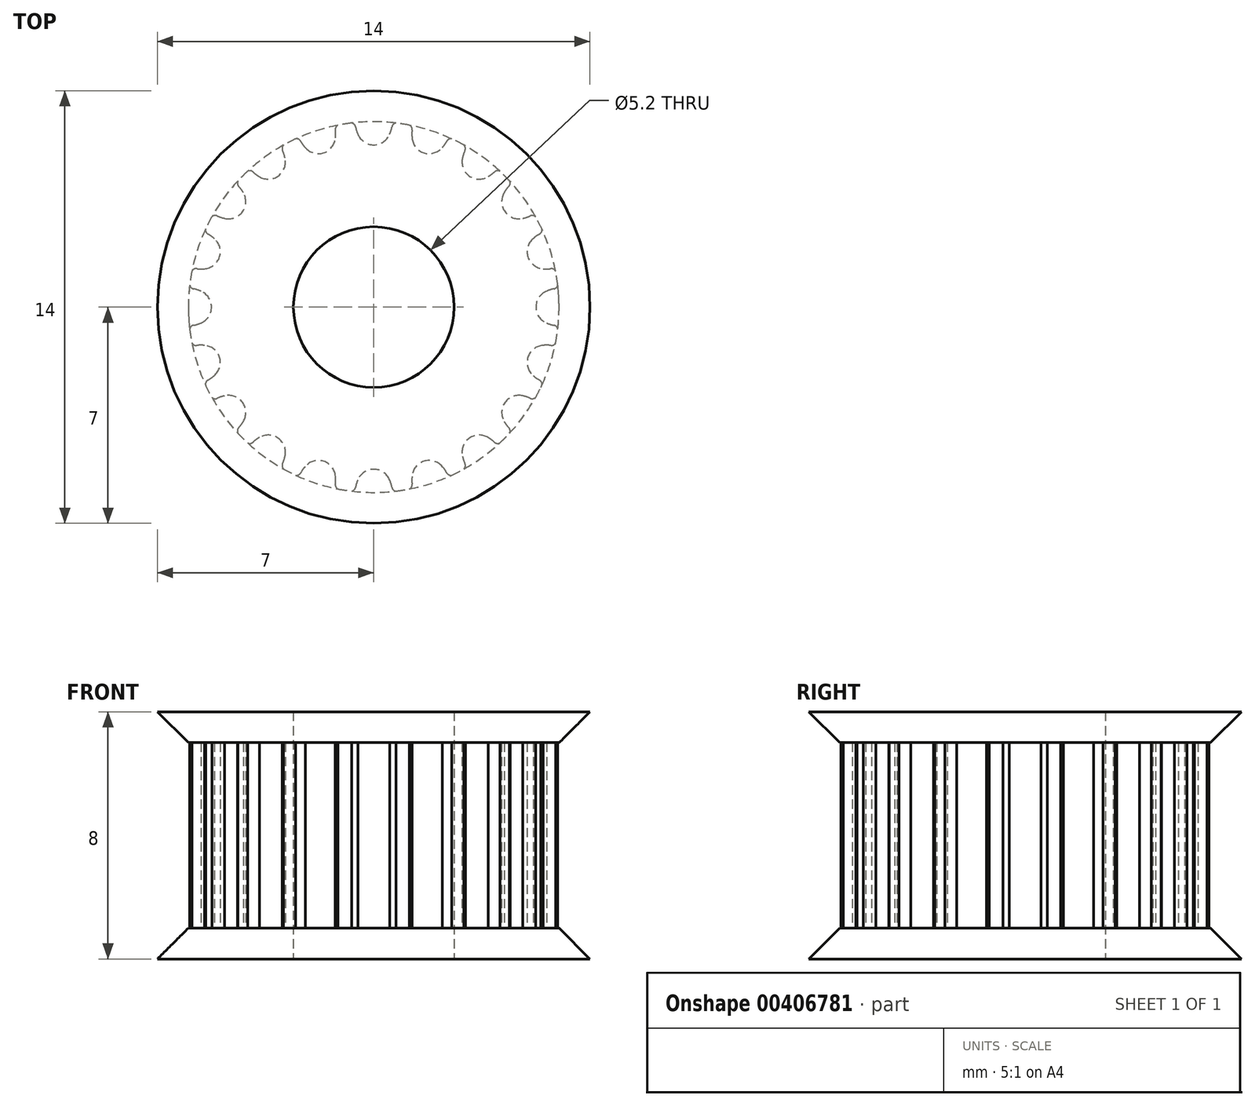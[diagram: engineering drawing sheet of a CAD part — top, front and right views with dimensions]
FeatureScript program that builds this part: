
annotation { "Feature Type Name" : "Feature", "Feature Type Description" : "" }
export const myFeature = defineFeature(function(context is Context, id is Id, definition is map)
    precondition{}
    {
        {
            var Q0;
            Q0=qCreatedBy(makeId("Top.planeOp"),FACE);
            var sketch = newSketch(context, id + "F0", { "sketchPlane" : qUnion([Q0])});
            skLineSegment(sketch, "E0", {"start": v(-19.17, 17.78) * mm, "end": v(-18.17, 17.78) * mm});
            skLineSegment(sketch, "E1", {"start": v(-18.17, 17.78) * mm, "end": v(-18.17, 18.4) * mm});
            skArc(sketch, "E2", {"start": v(-18.67, 18.85) * mm, "mid": v(-18.88, 19.07) * mm, "end": v(-19.17, 19.16) * mm});
            skArc(sketch, "E3", {"start": v(-18.58, 18.54) * mm, "mid": v(-18.61, 18.7) * mm, "end": v(-18.67, 18.85) * mm});
            skArc(sketch, "E4", {"start": v(-18.58, 18.54) * mm, "mid": v(-18.53, 18.44) * mm, "end": v(-18.43, 18.4) * mm});
            skLineSegment(sketch, "E5", {"start": v(-18.43, 18.4) * mm, "end": v(-18.17, 18.4) * mm});
            skArc(sketch, "E6.0.MirrorCS", {"start": v(-19.67, 18.85) * mm, "mid": v(-19.47, 19.07) * mm, "end": v(-19.17, 19.16) * mm});
            skArc(sketch, "E7.0.MirrorCS", {"start": v(-19.76, 18.54) * mm, "mid": v(-19.73, 18.7) * mm, "end": v(-19.67, 18.85) * mm});
            skArc(sketch, "E8.0.MirrorCS", {"start": v(-19.76, 18.54) * mm, "mid": v(-19.81, 18.44) * mm, "end": v(-19.91, 18.4) * mm});
            skLineSegment(sketch, "E9.0.MirrorCS", {"start": v(-19.91, 18.4) * mm, "end": v(-20.17, 18.4) * mm});
            skLineSegment(sketch, "E10.0.MirrorCS", {"start": v(-20.17, 17.78) * mm, "end": v(-20.17, 18.4) * mm});
            skLineSegment(sketch, "E11.0.MirrorCS", {"start": v(-19.17, 17.78) * mm, "end": v(-20.17, 17.78) * mm});
            skLineSegment(sketch, "E12.direction1", {"start": v(-20.17, 17.78) * mm, "end": v(-18.17, 17.78) * mm, "construction": true});
            skLineSegment(sketch, "E13", {"start": v(-20.17, 18.15) * mm, "end": v(-18.17, 18.15) * mm, "construction": true});
            skPoint(sketch, "E14", {"position": v(0, -5.25) * mm});
            skArc(sketch, "E15", {"start": v(0.51, -5.6) * mm, "mid": v(0, -5.25) * mm, "end": v(-0.51, -5.6) * mm});
            skArc(sketch, "E16", {"start": v(-0.51, -5.6) * mm, "mid": v(-0.56, -5.71) * mm, "end": v(-0.59, -5.83) * mm});
            skArc(sketch, "E17", {"start": v(0.59, -5.83) * mm, "mid": v(0.56, -5.71) * mm, "end": v(0.51, -5.6) * mm});
            skArc(sketch, "E18", {"start": v(0.72, -5.96) * mm, "mid": v(0.94, -5.93) * mm, "end": v(1.16, -5.89) * mm});
            skArc(sketch, "E19", {"start": v(0.59, -5.83) * mm, "mid": v(0.66, -5.94) * mm, "end": v(0.8, -5.95) * mm});
            skArc(sketch, "E20", {"start": v(-0.59, -5.83) * mm, "mid": v(-0.66, -5.94) * mm, "end": v(-0.8, -5.95) * mm});
            skArc(sketch, "E21.1.0", {"start": v(2.22, -5.16) * mm, "mid": v(1.62, -5) * mm, "end": v(1.24, -5.48) * mm});
            skPoint(sketch, "E21.1.1", {"position": v(1.62, -5) * mm});
            skArc(sketch, "E21.1.2", {"start": v(1.24, -5.48) * mm, "mid": v(1.23, -5.6) * mm, "end": v(1.24, -5.73) * mm});
            skArc(sketch, "E21.1.3", {"start": v(2.36, -5.37) * mm, "mid": v(2.47, -5.44) * mm, "end": v(2.6, -5.41) * mm});
            skArc(sketch, "E21.1.4", {"start": v(1.24, -5.73) * mm, "mid": v(1.2, -5.85) * mm, "end": v(1.08, -5.9) * mm});
            skArc(sketch, "E21.1.5", {"start": v(2.36, -5.37) * mm, "mid": v(2.3, -5.26) * mm, "end": v(2.22, -5.16) * mm});
            skArc(sketch, "E22.3.2.0", {"start": v(3.7, -4.22) * mm, "mid": v(3.09, -4.25) * mm, "end": v(2.87, -4.83) * mm});
            skPoint(sketch, "E22.4.2.0", {"position": v(3.09, -4.25) * mm});
            skArc(sketch, "E22.5.2.0", {"start": v(2.87, -4.83) * mm, "mid": v(2.9, -4.95) * mm, "end": v(2.95, -5.07) * mm});
            skArc(sketch, "E22.9.2.0", {"start": v(3.9, -4.37) * mm, "mid": v(4.03, -4.41) * mm, "end": v(4.14, -4.35) * mm});
            skArc(sketch, "E22.13.2.0", {"start": v(2.95, -5.07) * mm, "mid": v(2.95, -5.2) * mm, "end": v(2.85, -5.28) * mm});
            skArc(sketch, "E22.17.2.0", {"start": v(3.9, -4.37) * mm, "mid": v(3.81, -4.3) * mm, "end": v(3.7, -4.22) * mm});
            skArc(sketch, "E22.3.3.0", {"start": v(4.83, -2.87) * mm, "mid": v(4.25, -3.09) * mm, "end": v(4.22, -3.7) * mm});
            skPoint(sketch, "E22.4.3.0", {"position": v(4.25, -3.09) * mm});
            skArc(sketch, "E22.5.3.0", {"start": v(4.22, -3.7) * mm, "mid": v(4.3, -3.81) * mm, "end": v(4.37, -3.9) * mm});
            skArc(sketch, "E22.9.3.0", {"start": v(5.07, -2.95) * mm, "mid": v(5.2, -2.95) * mm, "end": v(5.28, -2.85) * mm});
            skArc(sketch, "E22.13.3.0", {"start": v(4.37, -3.9) * mm, "mid": v(4.41, -4.03) * mm, "end": v(4.35, -4.14) * mm});
            skArc(sketch, "E22.17.3.0", {"start": v(5.07, -2.95) * mm, "mid": v(4.95, -2.9) * mm, "end": v(4.83, -2.87) * mm});
            skArc(sketch, "E22.3.4.0", {"start": v(5.48, -1.24) * mm, "mid": v(5, -1.62) * mm, "end": v(5.16, -2.22) * mm});
            skPoint(sketch, "E22.4.4.0", {"position": v(5, -1.62) * mm});
            skArc(sketch, "E22.5.4.0", {"start": v(5.16, -2.22) * mm, "mid": v(5.26, -2.3) * mm, "end": v(5.37, -2.36) * mm});
            skArc(sketch, "E22.9.4.0", {"start": v(5.73, -1.24) * mm, "mid": v(5.85, -1.2) * mm, "end": v(5.9, -1.08) * mm});
            skArc(sketch, "E22.13.4.0", {"start": v(5.37, -2.36) * mm, "mid": v(5.44, -2.47) * mm, "end": v(5.41, -2.6) * mm});
            skArc(sketch, "E22.17.4.0", {"start": v(5.73, -1.24) * mm, "mid": v(5.6, -1.23) * mm, "end": v(5.48, -1.24) * mm});
            skArc(sketch, "E22.3.5.0", {"start": v(5.6, 0.51) * mm, "mid": v(5.25, 0) * mm, "end": v(5.6, -0.51) * mm});
            skPoint(sketch, "E22.4.5.0", {"position": v(5.25, 0) * mm});
            skArc(sketch, "E22.5.5.0", {"start": v(5.6, -0.51) * mm, "mid": v(5.71, -0.56) * mm, "end": v(5.83, -0.59) * mm});
            skArc(sketch, "E22.9.5.0", {"start": v(5.83, 0.59) * mm, "mid": v(5.94, 0.66) * mm, "end": v(5.95, 0.8) * mm});
            skArc(sketch, "E22.13.5.0", {"start": v(5.83, -0.59) * mm, "mid": v(5.94, -0.66) * mm, "end": v(5.95, -0.8) * mm});
            skArc(sketch, "E22.17.5.0", {"start": v(5.83, 0.59) * mm, "mid": v(5.71, 0.56) * mm, "end": v(5.6, 0.51) * mm});
            skArc(sketch, "E22.3.6.0", {"start": v(5.16, 2.22) * mm, "mid": v(5, 1.62) * mm, "end": v(5.48, 1.24) * mm});
            skPoint(sketch, "E22.4.6.0", {"position": v(5, 1.62) * mm});
            skArc(sketch, "E22.5.6.0", {"start": v(5.48, 1.24) * mm, "mid": v(5.6, 1.23) * mm, "end": v(5.73, 1.24) * mm});
            skArc(sketch, "E22.9.6.0", {"start": v(5.37, 2.36) * mm, "mid": v(5.44, 2.47) * mm, "end": v(5.41, 2.6) * mm});
            skArc(sketch, "E22.13.6.0", {"start": v(5.73, 1.24) * mm, "mid": v(5.85, 1.2) * mm, "end": v(5.9, 1.08) * mm});
            skArc(sketch, "E22.17.6.0", {"start": v(5.37, 2.36) * mm, "mid": v(5.26, 2.3) * mm, "end": v(5.16, 2.22) * mm});
            skArc(sketch, "E22.3.7.0", {"start": v(4.22, 3.7) * mm, "mid": v(4.25, 3.09) * mm, "end": v(4.83, 2.87) * mm});
            skPoint(sketch, "E22.4.7.0", {"position": v(4.25, 3.09) * mm});
            skArc(sketch, "E22.5.7.0", {"start": v(4.83, 2.87) * mm, "mid": v(4.95, 2.9) * mm, "end": v(5.07, 2.95) * mm});
            skArc(sketch, "E22.9.7.0", {"start": v(4.37, 3.9) * mm, "mid": v(4.41, 4.03) * mm, "end": v(4.35, 4.14) * mm});
            skArc(sketch, "E22.13.7.0", {"start": v(5.07, 2.95) * mm, "mid": v(5.2, 2.95) * mm, "end": v(5.28, 2.85) * mm});
            skArc(sketch, "E22.17.7.0", {"start": v(4.37, 3.9) * mm, "mid": v(4.3, 3.81) * mm, "end": v(4.22, 3.7) * mm});
            skArc(sketch, "E22.3.8.0", {"start": v(2.87, 4.83) * mm, "mid": v(3.09, 4.25) * mm, "end": v(3.7, 4.22) * mm});
            skPoint(sketch, "E22.4.8.0", {"position": v(3.09, 4.25) * mm});
            skArc(sketch, "E22.5.8.0", {"start": v(3.7, 4.22) * mm, "mid": v(3.81, 4.3) * mm, "end": v(3.9, 4.37) * mm});
            skArc(sketch, "E22.9.8.0", {"start": v(2.95, 5.07) * mm, "mid": v(2.95, 5.2) * mm, "end": v(2.85, 5.28) * mm});
            skArc(sketch, "E22.13.8.0", {"start": v(3.9, 4.37) * mm, "mid": v(4.03, 4.41) * mm, "end": v(4.14, 4.35) * mm});
            skArc(sketch, "E22.17.8.0", {"start": v(2.95, 5.07) * mm, "mid": v(2.9, 4.95) * mm, "end": v(2.87, 4.83) * mm});
            skArc(sketch, "E22.3.9.0", {"start": v(1.24, 5.48) * mm, "mid": v(1.62, 5) * mm, "end": v(2.22, 5.16) * mm});
            skPoint(sketch, "E22.4.9.0", {"position": v(1.62, 5) * mm});
            skArc(sketch, "E22.5.9.0", {"start": v(2.22, 5.16) * mm, "mid": v(2.3, 5.26) * mm, "end": v(2.36, 5.37) * mm});
            skArc(sketch, "E22.9.9.0", {"start": v(1.24, 5.73) * mm, "mid": v(1.2, 5.85) * mm, "end": v(1.08, 5.9) * mm});
            skArc(sketch, "E22.13.9.0", {"start": v(2.36, 5.37) * mm, "mid": v(2.47, 5.44) * mm, "end": v(2.6, 5.41) * mm});
            skArc(sketch, "E22.17.9.0", {"start": v(1.24, 5.73) * mm, "mid": v(1.23, 5.6) * mm, "end": v(1.24, 5.48) * mm});
            skArc(sketch, "E22.3.10.0", {"start": v(-0.51, 5.6) * mm, "mid": v(0, 5.25) * mm, "end": v(0.51, 5.6) * mm});
            skPoint(sketch, "E22.4.10.0", {"position": v(0, 5.25) * mm});
            skArc(sketch, "E22.5.10.0", {"start": v(0.51, 5.6) * mm, "mid": v(0.56, 5.71) * mm, "end": v(0.59, 5.83) * mm});
            skArc(sketch, "E22.9.10.0", {"start": v(-0.59, 5.83) * mm, "mid": v(-0.66, 5.94) * mm, "end": v(-0.8, 5.95) * mm});
            skArc(sketch, "E22.13.10.0", {"start": v(0.59, 5.83) * mm, "mid": v(0.66, 5.94) * mm, "end": v(0.8, 5.95) * mm});
            skArc(sketch, "E22.17.10.0", {"start": v(-0.59, 5.83) * mm, "mid": v(-0.56, 5.71) * mm, "end": v(-0.51, 5.6) * mm});
            skArc(sketch, "E22.3.11.0", {"start": v(-2.22, 5.16) * mm, "mid": v(-1.62, 5) * mm, "end": v(-1.24, 5.48) * mm});
            skPoint(sketch, "E22.4.11.0", {"position": v(-1.62, 5) * mm});
            skArc(sketch, "E22.5.11.0", {"start": v(-1.24, 5.48) * mm, "mid": v(-1.23, 5.6) * mm, "end": v(-1.24, 5.73) * mm});
            skArc(sketch, "E22.9.11.0", {"start": v(-2.36, 5.37) * mm, "mid": v(-2.47, 5.44) * mm, "end": v(-2.6, 5.41) * mm});
            skArc(sketch, "E22.13.11.0", {"start": v(-1.24, 5.73) * mm, "mid": v(-1.2, 5.85) * mm, "end": v(-1.08, 5.9) * mm});
            skArc(sketch, "E22.17.11.0", {"start": v(-2.36, 5.37) * mm, "mid": v(-2.3, 5.26) * mm, "end": v(-2.22, 5.16) * mm});
            skArc(sketch, "E22.3.12.0", {"start": v(-3.7, 4.22) * mm, "mid": v(-3.09, 4.25) * mm, "end": v(-2.87, 4.83) * mm});
            skPoint(sketch, "E22.4.12.0", {"position": v(-3.09, 4.25) * mm});
            skArc(sketch, "E22.5.12.0", {"start": v(-2.87, 4.83) * mm, "mid": v(-2.9, 4.95) * mm, "end": v(-2.95, 5.07) * mm});
            skArc(sketch, "E22.9.12.0", {"start": v(-3.9, 4.37) * mm, "mid": v(-4.03, 4.41) * mm, "end": v(-4.14, 4.35) * mm});
            skArc(sketch, "E22.13.12.0", {"start": v(-2.95, 5.07) * mm, "mid": v(-2.95, 5.2) * mm, "end": v(-2.85, 5.28) * mm});
            skArc(sketch, "E22.17.12.0", {"start": v(-3.9, 4.37) * mm, "mid": v(-3.81, 4.3) * mm, "end": v(-3.7, 4.22) * mm});
            skArc(sketch, "E22.3.13.0", {"start": v(-4.83, 2.87) * mm, "mid": v(-4.25, 3.09) * mm, "end": v(-4.22, 3.7) * mm});
            skPoint(sketch, "E22.4.13.0", {"position": v(-4.25, 3.09) * mm});
            skArc(sketch, "E22.5.13.0", {"start": v(-4.22, 3.7) * mm, "mid": v(-4.3, 3.81) * mm, "end": v(-4.37, 3.9) * mm});
            skArc(sketch, "E22.9.13.0", {"start": v(-5.07, 2.95) * mm, "mid": v(-5.2, 2.95) * mm, "end": v(-5.28, 2.85) * mm});
            skArc(sketch, "E22.13.13.0", {"start": v(-4.37, 3.9) * mm, "mid": v(-4.41, 4.03) * mm, "end": v(-4.35, 4.14) * mm});
            skArc(sketch, "E22.17.13.0", {"start": v(-5.07, 2.95) * mm, "mid": v(-4.95, 2.9) * mm, "end": v(-4.83, 2.87) * mm});
            skArc(sketch, "E22.3.14.0", {"start": v(-5.48, 1.24) * mm, "mid": v(-5, 1.62) * mm, "end": v(-5.16, 2.22) * mm});
            skPoint(sketch, "E22.4.14.0", {"position": v(-5, 1.62) * mm});
            skArc(sketch, "E22.5.14.0", {"start": v(-5.16, 2.22) * mm, "mid": v(-5.26, 2.3) * mm, "end": v(-5.37, 2.36) * mm});
            skArc(sketch, "E22.9.14.0", {"start": v(-5.73, 1.24) * mm, "mid": v(-5.85, 1.2) * mm, "end": v(-5.9, 1.08) * mm});
            skArc(sketch, "E22.13.14.0", {"start": v(-5.37, 2.36) * mm, "mid": v(-5.44, 2.47) * mm, "end": v(-5.41, 2.6) * mm});
            skArc(sketch, "E22.17.14.0", {"start": v(-5.73, 1.24) * mm, "mid": v(-5.6, 1.23) * mm, "end": v(-5.48, 1.24) * mm});
            skArc(sketch, "E22.3.15.0", {"start": v(-5.6, -0.51) * mm, "mid": v(-5.25, 0) * mm, "end": v(-5.6, 0.51) * mm});
            skPoint(sketch, "E22.4.15.0", {"position": v(-5.25, 0) * mm});
            skArc(sketch, "E22.5.15.0", {"start": v(-5.6, 0.51) * mm, "mid": v(-5.71, 0.56) * mm, "end": v(-5.83, 0.59) * mm});
            skArc(sketch, "E22.9.15.0", {"start": v(-5.83, -0.59) * mm, "mid": v(-5.94, -0.66) * mm, "end": v(-5.95, -0.8) * mm});
            skArc(sketch, "E22.13.15.0", {"start": v(-5.83, 0.59) * mm, "mid": v(-5.94, 0.66) * mm, "end": v(-5.95, 0.8) * mm});
            skArc(sketch, "E22.17.15.0", {"start": v(-5.83, -0.59) * mm, "mid": v(-5.71, -0.56) * mm, "end": v(-5.6, -0.51) * mm});
            skArc(sketch, "E22.3.16.0", {"start": v(-5.16, -2.22) * mm, "mid": v(-5, -1.62) * mm, "end": v(-5.48, -1.24) * mm});
            skPoint(sketch, "E22.4.16.0", {"position": v(-5, -1.62) * mm});
            skArc(sketch, "E22.5.16.0", {"start": v(-5.48, -1.24) * mm, "mid": v(-5.6, -1.23) * mm, "end": v(-5.73, -1.24) * mm});
            skArc(sketch, "E22.9.16.0", {"start": v(-5.37, -2.36) * mm, "mid": v(-5.44, -2.47) * mm, "end": v(-5.41, -2.6) * mm});
            skArc(sketch, "E22.13.16.0", {"start": v(-5.73, -1.24) * mm, "mid": v(-5.85, -1.2) * mm, "end": v(-5.9, -1.08) * mm});
            skArc(sketch, "E22.17.16.0", {"start": v(-5.37, -2.36) * mm, "mid": v(-5.26, -2.3) * mm, "end": v(-5.16, -2.22) * mm});
            skArc(sketch, "E22.3.17.0", {"start": v(-4.22, -3.7) * mm, "mid": v(-4.25, -3.09) * mm, "end": v(-4.83, -2.87) * mm});
            skPoint(sketch, "E22.4.17.0", {"position": v(-4.25, -3.09) * mm});
            skArc(sketch, "E22.5.17.0", {"start": v(-4.83, -2.87) * mm, "mid": v(-4.95, -2.9) * mm, "end": v(-5.07, -2.95) * mm});
            skArc(sketch, "E22.9.17.0", {"start": v(-4.37, -3.9) * mm, "mid": v(-4.41, -4.03) * mm, "end": v(-4.35, -4.14) * mm});
            skArc(sketch, "E22.13.17.0", {"start": v(-5.07, -2.95) * mm, "mid": v(-5.2, -2.95) * mm, "end": v(-5.28, -2.85) * mm});
            skArc(sketch, "E22.17.17.0", {"start": v(-4.37, -3.9) * mm, "mid": v(-4.3, -3.81) * mm, "end": v(-4.22, -3.7) * mm});
            skArc(sketch, "E22.3.18.0", {"start": v(-2.87, -4.83) * mm, "mid": v(-3.09, -4.25) * mm, "end": v(-3.7, -4.22) * mm});
            skPoint(sketch, "E22.4.18.0", {"position": v(-3.09, -4.25) * mm});
            skArc(sketch, "E22.5.18.0", {"start": v(-3.7, -4.22) * mm, "mid": v(-3.81, -4.3) * mm, "end": v(-3.9, -4.37) * mm});
            skArc(sketch, "E22.9.18.0", {"start": v(-2.95, -5.07) * mm, "mid": v(-2.95, -5.2) * mm, "end": v(-2.85, -5.28) * mm});
            skArc(sketch, "E22.13.18.0", {"start": v(-3.9, -4.37) * mm, "mid": v(-4.03, -4.41) * mm, "end": v(-4.14, -4.35) * mm});
            skArc(sketch, "E22.17.18.0", {"start": v(-2.95, -5.07) * mm, "mid": v(-2.9, -4.95) * mm, "end": v(-2.87, -4.83) * mm});
            skArc(sketch, "E22.3.19.0", {"start": v(-1.24, -5.48) * mm, "mid": v(-1.62, -5) * mm, "end": v(-2.22, -5.16) * mm});
            skPoint(sketch, "E22.4.19.0", {"position": v(-1.62, -5) * mm});
            skArc(sketch, "E22.5.19.0", {"start": v(-2.22, -5.16) * mm, "mid": v(-2.3, -5.26) * mm, "end": v(-2.36, -5.37) * mm});
            skArc(sketch, "E22.9.19.0", {"start": v(-1.24, -5.73) * mm, "mid": v(-1.2, -5.85) * mm, "end": v(-1.08, -5.9) * mm});
            skArc(sketch, "E22.13.19.0", {"start": v(-2.36, -5.37) * mm, "mid": v(-2.47, -5.44) * mm, "end": v(-2.6, -5.41) * mm});
            skArc(sketch, "E22.17.19.0", {"start": v(-1.24, -5.73) * mm, "mid": v(-1.23, -5.6) * mm, "end": v(-1.24, -5.48) * mm});
            skArc(sketch, "E23.trimOffspring", {"start": v(2.52, -5.44) * mm, "mid": v(2.72, -5.35) * mm, "end": v(2.92, -5.24) * mm});
            skArc(sketch, "E24.trimOffspring", {"start": v(4.08, -4.4) * mm, "mid": v(4.24, -4.24) * mm, "end": v(4.4, -4.08) * mm});
            skArc(sketch, "E25.trimOffspring", {"start": v(5.24, -2.92) * mm, "mid": v(5.33, -2.76) * mm, "end": v(5.41, -2.6) * mm});
            skArc(sketch, "E26.trimOffspring", {"start": v(5.89, -1.16) * mm, "mid": v(5.93, -0.94) * mm, "end": v(5.96, -0.72) * mm});
            skArc(sketch, "E27.trimOffspring", {"start": v(5.44, 2.52) * mm, "mid": v(5.35, 2.72) * mm, "end": v(5.24, 2.92) * mm});
            skArc(sketch, "E28.trimOffspring", {"start": v(4.4, 4.08) * mm, "mid": v(4.24, 4.24) * mm, "end": v(4.08, 4.4) * mm});
            skArc(sketch, "E29.trimOffspring", {"start": v(5.96, 0.72) * mm, "mid": v(5.93, 0.94) * mm, "end": v(5.89, 1.16) * mm});
            skArc(sketch, "E30.trimOffspring", {"start": v(2.92, 5.24) * mm, "mid": v(2.72, 5.35) * mm, "end": v(2.52, 5.44) * mm});
            skArc(sketch, "E31.trimOffspring", {"start": v(1.16, 5.89) * mm, "mid": v(0.94, 5.93) * mm, "end": v(0.72, 5.96) * mm});
            skArc(sketch, "E32.trimOffspring", {"start": v(-0.72, 5.96) * mm, "mid": v(-0.94, 5.93) * mm, "end": v(-1.16, 5.89) * mm});
            skArc(sketch, "E33.trimOffspring", {"start": v(-2.52, 5.44) * mm, "mid": v(-2.72, 5.35) * mm, "end": v(-2.92, 5.24) * mm});
            skArc(sketch, "E34.trimOffspring", {"start": v(-4.08, 4.4) * mm, "mid": v(-4.24, 4.24) * mm, "end": v(-4.4, 4.08) * mm});
            skArc(sketch, "E35.trimOffspring", {"start": v(-5.24, 2.92) * mm, "mid": v(-5.35, 2.72) * mm, "end": v(-5.44, 2.52) * mm});
            skArc(sketch, "E36.trimOffspring", {"start": v(-5.89, 1.16) * mm, "mid": v(-5.93, 0.94) * mm, "end": v(-5.96, 0.72) * mm});
            skArc(sketch, "E37.trimOffspring", {"start": v(-5.96, -0.72) * mm, "mid": v(-5.93, -0.94) * mm, "end": v(-5.89, -1.16) * mm});
            skArc(sketch, "E38.trimOffspring", {"start": v(-5.44, -2.52) * mm, "mid": v(-5.35, -2.72) * mm, "end": v(-5.24, -2.92) * mm});
            skArc(sketch, "E39.trimOffspring", {"start": v(-4.4, -4.08) * mm, "mid": v(-4.24, -4.24) * mm, "end": v(-4.08, -4.4) * mm});
            skArc(sketch, "E40.trimOffspring", {"start": v(-2.92, -5.24) * mm, "mid": v(-2.72, -5.35) * mm, "end": v(-2.52, -5.44) * mm});
            skArc(sketch, "E41.trimOffspring", {"start": v(-1.16, -5.89) * mm, "mid": v(-0.94, -5.93) * mm, "end": v(-0.72, -5.96) * mm});
            skSolve(sketch);
        }
        {
            var Q0;
            Q0=makeQuery(id+"F0.imprint","IMPRINT",FACE,{"disambiguationData":[TD([[makeQuery(id+"F0.imprint","IMPRINT",EDGE,{"derivedFrom":sQuery(id+"F0.wireOp",EDGE,"E15")}),-1.0]])]});
            extrude(context, id + "F1", {"entities" : qUnion([Q0]), "depth" : 6 * mm});
        }
        {
            var Q0;
            Q0=makeQuery(id+"F1.opExtrude","CAP_FACE",FACE,{"disambiguationData":[OSD([sQuery(id+"F0.wireOp",EDGE,"E15"),sQuery(id+"F0.wireOp",EDGE,"E16"),sQuery(id+"F0.wireOp",EDGE,"E17"),sQuery(id+"F0.wireOp",EDGE,"E18"),sQuery(id+"F0.wireOp",EDGE,"E19"),sQuery(id+"F0.wireOp",EDGE,"E20"),sQuery(id+"F0.wireOp",EDGE,"E21.1.0"),sQuery(id+"F0.wireOp",EDGE,"E21.1.2"),sQuery(id+"F0.wireOp",EDGE,"E21.1.3"),sQuery(id+"F0.wireOp",EDGE,"E21.1.4"),sQuery(id+"F0.wireOp",EDGE,"E21.1.5"),sQuery(id+"F0.wireOp",EDGE,"E22.3.2.0"),sQuery(id+"F0.wireOp",EDGE,"E22.5.2.0"),sQuery(id+"F0.wireOp",EDGE,"E22.9.2.0"),sQuery(id+"F0.wireOp",EDGE,"E22.13.2.0"),sQuery(id+"F0.wireOp",EDGE,"E22.17.2.0"),sQuery(id+"F0.wireOp",EDGE,"E22.3.3.0"),sQuery(id+"F0.wireOp",EDGE,"E22.5.3.0"),sQuery(id+"F0.wireOp",EDGE,"E22.9.3.0"),sQuery(id+"F0.wireOp",EDGE,"E22.13.3.0"),sQuery(id+"F0.wireOp",EDGE,"E22.17.3.0"),sQuery(id+"F0.wireOp",EDGE,"E22.3.4.0"),sQuery(id+"F0.wireOp",EDGE,"E22.5.4.0"),sQuery(id+"F0.wireOp",EDGE,"E22.9.4.0"),sQuery(id+"F0.wireOp",EDGE,"E22.13.4.0"),sQuery(id+"F0.wireOp",EDGE,"E22.17.4.0"),sQuery(id+"F0.wireOp",EDGE,"E22.3.5.0"),sQuery(id+"F0.wireOp",EDGE,"E22.5.5.0"),sQuery(id+"F0.wireOp",EDGE,"E22.9.5.0"),sQuery(id+"F0.wireOp",EDGE,"E22.13.5.0"),sQuery(id+"F0.wireOp",EDGE,"E22.17.5.0"),sQuery(id+"F0.wireOp",EDGE,"E22.3.6.0"),sQuery(id+"F0.wireOp",EDGE,"E22.5.6.0"),sQuery(id+"F0.wireOp",EDGE,"E22.9.6.0"),sQuery(id+"F0.wireOp",EDGE,"E22.13.6.0"),sQuery(id+"F0.wireOp",EDGE,"E22.17.6.0"),sQuery(id+"F0.wireOp",EDGE,"E22.3.7.0"),sQuery(id+"F0.wireOp",EDGE,"E22.5.7.0"),sQuery(id+"F0.wireOp",EDGE,"E22.9.7.0"),sQuery(id+"F0.wireOp",EDGE,"E22.13.7.0"),sQuery(id+"F0.wireOp",EDGE,"E22.17.7.0"),sQuery(id+"F0.wireOp",EDGE,"E22.3.8.0"),sQuery(id+"F0.wireOp",EDGE,"E22.5.8.0"),sQuery(id+"F0.wireOp",EDGE,"E22.9.8.0"),sQuery(id+"F0.wireOp",EDGE,"E22.13.8.0"),sQuery(id+"F0.wireOp",EDGE,"E22.17.8.0"),sQuery(id+"F0.wireOp",EDGE,"E22.3.9.0"),sQuery(id+"F0.wireOp",EDGE,"E22.5.9.0"),sQuery(id+"F0.wireOp",EDGE,"E22.9.9.0"),sQuery(id+"F0.wireOp",EDGE,"E22.13.9.0"),sQuery(id+"F0.wireOp",EDGE,"E22.17.9.0"),sQuery(id+"F0.wireOp",EDGE,"E22.3.10.0"),sQuery(id+"F0.wireOp",EDGE,"E22.5.10.0"),sQuery(id+"F0.wireOp",EDGE,"E22.9.10.0"),sQuery(id+"F0.wireOp",EDGE,"E22.13.10.0"),sQuery(id+"F0.wireOp",EDGE,"E22.17.10.0"),sQuery(id+"F0.wireOp",EDGE,"E22.3.11.0"),sQuery(id+"F0.wireOp",EDGE,"E22.5.11.0"),sQuery(id+"F0.wireOp",EDGE,"E22.9.11.0"),sQuery(id+"F0.wireOp",EDGE,"E22.13.11.0"),sQuery(id+"F0.wireOp",EDGE,"E22.17.11.0"),sQuery(id+"F0.wireOp",EDGE,"E22.3.12.0"),sQuery(id+"F0.wireOp",EDGE,"E22.5.12.0"),sQuery(id+"F0.wireOp",EDGE,"E22.9.12.0"),sQuery(id+"F0.wireOp",EDGE,"E22.13.12.0"),sQuery(id+"F0.wireOp",EDGE,"E22.17.12.0"),sQuery(id+"F0.wireOp",EDGE,"E22.3.13.0"),sQuery(id+"F0.wireOp",EDGE,"E22.5.13.0"),sQuery(id+"F0.wireOp",EDGE,"E22.9.13.0"),sQuery(id+"F0.wireOp",EDGE,"E22.13.13.0"),sQuery(id+"F0.wireOp",EDGE,"E22.17.13.0"),sQuery(id+"F0.wireOp",EDGE,"E22.3.14.0"),sQuery(id+"F0.wireOp",EDGE,"E22.5.14.0"),sQuery(id+"F0.wireOp",EDGE,"E22.9.14.0"),sQuery(id+"F0.wireOp",EDGE,"E22.13.14.0"),sQuery(id+"F0.wireOp",EDGE,"E22.17.14.0"),sQuery(id+"F0.wireOp",EDGE,"E22.3.15.0"),sQuery(id+"F0.wireOp",EDGE,"E22.5.15.0"),sQuery(id+"F0.wireOp",EDGE,"E22.9.15.0"),sQuery(id+"F0.wireOp",EDGE,"E22.13.15.0"),sQuery(id+"F0.wireOp",EDGE,"E22.17.15.0"),sQuery(id+"F0.wireOp",EDGE,"E22.3.16.0"),sQuery(id+"F0.wireOp",EDGE,"E22.5.16.0"),sQuery(id+"F0.wireOp",EDGE,"E22.9.16.0"),sQuery(id+"F0.wireOp",EDGE,"E22.13.16.0"),sQuery(id+"F0.wireOp",EDGE,"E22.17.16.0"),sQuery(id+"F0.wireOp",EDGE,"E22.3.17.0"),sQuery(id+"F0.wireOp",EDGE,"E22.5.17.0"),sQuery(id+"F0.wireOp",EDGE,"E22.9.17.0"),sQuery(id+"F0.wireOp",EDGE,"E22.13.17.0"),sQuery(id+"F0.wireOp",EDGE,"E22.17.17.0"),sQuery(id+"F0.wireOp",EDGE,"E22.3.18.0"),sQuery(id+"F0.wireOp",EDGE,"E22.5.18.0"),sQuery(id+"F0.wireOp",EDGE,"E22.9.18.0"),sQuery(id+"F0.wireOp",EDGE,"E22.13.18.0"),sQuery(id+"F0.wireOp",EDGE,"E22.17.18.0"),sQuery(id+"F0.wireOp",EDGE,"E22.3.19.0"),sQuery(id+"F0.wireOp",EDGE,"E22.5.19.0"),sQuery(id+"F0.wireOp",EDGE,"E22.9.19.0"),sQuery(id+"F0.wireOp",EDGE,"E22.13.19.0"),sQuery(id+"F0.wireOp",EDGE,"E22.17.19.0"),sQuery(id+"F0.wireOp",EDGE,"E23.trimOffspring"),sQuery(id+"F0.wireOp",EDGE,"E24.trimOffspring"),sQuery(id+"F0.wireOp",EDGE,"E25.trimOffspring"),sQuery(id+"F0.wireOp",EDGE,"E26.trimOffspring"),sQuery(id+"F0.wireOp",EDGE,"E27.trimOffspring"),sQuery(id+"F0.wireOp",EDGE,"E28.trimOffspring"),sQuery(id+"F0.wireOp",EDGE,"E29.trimOffspring"),sQuery(id+"F0.wireOp",EDGE,"E30.trimOffspring"),sQuery(id+"F0.wireOp",EDGE,"E31.trimOffspring"),sQuery(id+"F0.wireOp",EDGE,"E32.trimOffspring"),sQuery(id+"F0.wireOp",EDGE,"E33.trimOffspring"),sQuery(id+"F0.wireOp",EDGE,"E34.trimOffspring"),sQuery(id+"F0.wireOp",EDGE,"E35.trimOffspring"),sQuery(id+"F0.wireOp",EDGE,"E36.trimOffspring"),sQuery(id+"F0.wireOp",EDGE,"E37.trimOffspring"),sQuery(id+"F0.wireOp",EDGE,"E38.trimOffspring"),sQuery(id+"F0.wireOp",EDGE,"E39.trimOffspring"),sQuery(id+"F0.wireOp",EDGE,"E40.trimOffspring"),sQuery(id+"F0.wireOp",EDGE,"E41.trimOffspring")])],"isStart":false});
            var sketch = newSketch(context, id + "F2", { "sketchPlane" : qUnion([Q0])});
            skCircle(sketch, "E42", {"center": v(0, 0) * mm, "radius": 7 * mm});
            skSolve(sketch);
        }
        {
            var Q0;
            Q0=qSketchRegion(id+"F2",true);
            extrude(context, id + "F3", {"entities" : qUnion([Q0]), "operationType" : NewBodyOperationType.ADD, "depth" : 1 * mm});
        }
        {
            var Q0;
            Q0=makeQuery(id+"F1.opExtrude","CAP_FACE",FACE,{"disambiguationData":[OSD([sQuery(id+"F0.wireOp",EDGE,"E15"),sQuery(id+"F0.wireOp",EDGE,"E16"),sQuery(id+"F0.wireOp",EDGE,"E17"),sQuery(id+"F0.wireOp",EDGE,"E18"),sQuery(id+"F0.wireOp",EDGE,"E19"),sQuery(id+"F0.wireOp",EDGE,"E20"),sQuery(id+"F0.wireOp",EDGE,"E21.1.0"),sQuery(id+"F0.wireOp",EDGE,"E21.1.2"),sQuery(id+"F0.wireOp",EDGE,"E21.1.3"),sQuery(id+"F0.wireOp",EDGE,"E21.1.4"),sQuery(id+"F0.wireOp",EDGE,"E21.1.5"),sQuery(id+"F0.wireOp",EDGE,"E22.3.2.0"),sQuery(id+"F0.wireOp",EDGE,"E22.5.2.0"),sQuery(id+"F0.wireOp",EDGE,"E22.9.2.0"),sQuery(id+"F0.wireOp",EDGE,"E22.13.2.0"),sQuery(id+"F0.wireOp",EDGE,"E22.17.2.0"),sQuery(id+"F0.wireOp",EDGE,"E22.3.3.0"),sQuery(id+"F0.wireOp",EDGE,"E22.5.3.0"),sQuery(id+"F0.wireOp",EDGE,"E22.9.3.0"),sQuery(id+"F0.wireOp",EDGE,"E22.13.3.0"),sQuery(id+"F0.wireOp",EDGE,"E22.17.3.0"),sQuery(id+"F0.wireOp",EDGE,"E22.3.4.0"),sQuery(id+"F0.wireOp",EDGE,"E22.5.4.0"),sQuery(id+"F0.wireOp",EDGE,"E22.9.4.0"),sQuery(id+"F0.wireOp",EDGE,"E22.13.4.0"),sQuery(id+"F0.wireOp",EDGE,"E22.17.4.0"),sQuery(id+"F0.wireOp",EDGE,"E22.3.5.0"),sQuery(id+"F0.wireOp",EDGE,"E22.5.5.0"),sQuery(id+"F0.wireOp",EDGE,"E22.9.5.0"),sQuery(id+"F0.wireOp",EDGE,"E22.13.5.0"),sQuery(id+"F0.wireOp",EDGE,"E22.17.5.0"),sQuery(id+"F0.wireOp",EDGE,"E22.3.6.0"),sQuery(id+"F0.wireOp",EDGE,"E22.5.6.0"),sQuery(id+"F0.wireOp",EDGE,"E22.9.6.0"),sQuery(id+"F0.wireOp",EDGE,"E22.13.6.0"),sQuery(id+"F0.wireOp",EDGE,"E22.17.6.0"),sQuery(id+"F0.wireOp",EDGE,"E22.3.7.0"),sQuery(id+"F0.wireOp",EDGE,"E22.5.7.0"),sQuery(id+"F0.wireOp",EDGE,"E22.9.7.0"),sQuery(id+"F0.wireOp",EDGE,"E22.13.7.0"),sQuery(id+"F0.wireOp",EDGE,"E22.17.7.0"),sQuery(id+"F0.wireOp",EDGE,"E22.3.8.0"),sQuery(id+"F0.wireOp",EDGE,"E22.5.8.0"),sQuery(id+"F0.wireOp",EDGE,"E22.9.8.0"),sQuery(id+"F0.wireOp",EDGE,"E22.13.8.0"),sQuery(id+"F0.wireOp",EDGE,"E22.17.8.0"),sQuery(id+"F0.wireOp",EDGE,"E22.3.9.0"),sQuery(id+"F0.wireOp",EDGE,"E22.5.9.0"),sQuery(id+"F0.wireOp",EDGE,"E22.9.9.0"),sQuery(id+"F0.wireOp",EDGE,"E22.13.9.0"),sQuery(id+"F0.wireOp",EDGE,"E22.17.9.0"),sQuery(id+"F0.wireOp",EDGE,"E22.3.10.0"),sQuery(id+"F0.wireOp",EDGE,"E22.5.10.0"),sQuery(id+"F0.wireOp",EDGE,"E22.9.10.0"),sQuery(id+"F0.wireOp",EDGE,"E22.13.10.0"),sQuery(id+"F0.wireOp",EDGE,"E22.17.10.0"),sQuery(id+"F0.wireOp",EDGE,"E22.3.11.0"),sQuery(id+"F0.wireOp",EDGE,"E22.5.11.0"),sQuery(id+"F0.wireOp",EDGE,"E22.9.11.0"),sQuery(id+"F0.wireOp",EDGE,"E22.13.11.0"),sQuery(id+"F0.wireOp",EDGE,"E22.17.11.0"),sQuery(id+"F0.wireOp",EDGE,"E22.3.12.0"),sQuery(id+"F0.wireOp",EDGE,"E22.5.12.0"),sQuery(id+"F0.wireOp",EDGE,"E22.9.12.0"),sQuery(id+"F0.wireOp",EDGE,"E22.13.12.0"),sQuery(id+"F0.wireOp",EDGE,"E22.17.12.0"),sQuery(id+"F0.wireOp",EDGE,"E22.3.13.0"),sQuery(id+"F0.wireOp",EDGE,"E22.5.13.0"),sQuery(id+"F0.wireOp",EDGE,"E22.9.13.0"),sQuery(id+"F0.wireOp",EDGE,"E22.13.13.0"),sQuery(id+"F0.wireOp",EDGE,"E22.17.13.0"),sQuery(id+"F0.wireOp",EDGE,"E22.3.14.0"),sQuery(id+"F0.wireOp",EDGE,"E22.5.14.0"),sQuery(id+"F0.wireOp",EDGE,"E22.9.14.0"),sQuery(id+"F0.wireOp",EDGE,"E22.13.14.0"),sQuery(id+"F0.wireOp",EDGE,"E22.17.14.0"),sQuery(id+"F0.wireOp",EDGE,"E22.3.15.0"),sQuery(id+"F0.wireOp",EDGE,"E22.5.15.0"),sQuery(id+"F0.wireOp",EDGE,"E22.9.15.0"),sQuery(id+"F0.wireOp",EDGE,"E22.13.15.0"),sQuery(id+"F0.wireOp",EDGE,"E22.17.15.0"),sQuery(id+"F0.wireOp",EDGE,"E22.3.16.0"),sQuery(id+"F0.wireOp",EDGE,"E22.5.16.0"),sQuery(id+"F0.wireOp",EDGE,"E22.9.16.0"),sQuery(id+"F0.wireOp",EDGE,"E22.13.16.0"),sQuery(id+"F0.wireOp",EDGE,"E22.17.16.0"),sQuery(id+"F0.wireOp",EDGE,"E22.3.17.0"),sQuery(id+"F0.wireOp",EDGE,"E22.5.17.0"),sQuery(id+"F0.wireOp",EDGE,"E22.9.17.0"),sQuery(id+"F0.wireOp",EDGE,"E22.13.17.0"),sQuery(id+"F0.wireOp",EDGE,"E22.17.17.0"),sQuery(id+"F0.wireOp",EDGE,"E22.3.18.0"),sQuery(id+"F0.wireOp",EDGE,"E22.5.18.0"),sQuery(id+"F0.wireOp",EDGE,"E22.9.18.0"),sQuery(id+"F0.wireOp",EDGE,"E22.13.18.0"),sQuery(id+"F0.wireOp",EDGE,"E22.17.18.0"),sQuery(id+"F0.wireOp",EDGE,"E22.3.19.0"),sQuery(id+"F0.wireOp",EDGE,"E22.5.19.0"),sQuery(id+"F0.wireOp",EDGE,"E22.9.19.0"),sQuery(id+"F0.wireOp",EDGE,"E22.13.19.0"),sQuery(id+"F0.wireOp",EDGE,"E22.17.19.0"),sQuery(id+"F0.wireOp",EDGE,"E23.trimOffspring"),sQuery(id+"F0.wireOp",EDGE,"E24.trimOffspring"),sQuery(id+"F0.wireOp",EDGE,"E25.trimOffspring"),sQuery(id+"F0.wireOp",EDGE,"E26.trimOffspring"),sQuery(id+"F0.wireOp",EDGE,"E27.trimOffspring"),sQuery(id+"F0.wireOp",EDGE,"E28.trimOffspring"),sQuery(id+"F0.wireOp",EDGE,"E29.trimOffspring"),sQuery(id+"F0.wireOp",EDGE,"E30.trimOffspring"),sQuery(id+"F0.wireOp",EDGE,"E31.trimOffspring"),sQuery(id+"F0.wireOp",EDGE,"E32.trimOffspring"),sQuery(id+"F0.wireOp",EDGE,"E33.trimOffspring"),sQuery(id+"F0.wireOp",EDGE,"E34.trimOffspring"),sQuery(id+"F0.wireOp",EDGE,"E35.trimOffspring"),sQuery(id+"F0.wireOp",EDGE,"E36.trimOffspring"),sQuery(id+"F0.wireOp",EDGE,"E37.trimOffspring"),sQuery(id+"F0.wireOp",EDGE,"E38.trimOffspring"),sQuery(id+"F0.wireOp",EDGE,"E39.trimOffspring"),sQuery(id+"F0.wireOp",EDGE,"E40.trimOffspring"),sQuery(id+"F0.wireOp",EDGE,"E41.trimOffspring")])],"isStart":true});
            var sketch = newSketch(context, id + "F4", { "sketchPlane" : qUnion([Q0])});
            skCircle(sketch, "E43", {"center": v(0, 0) * mm, "radius": 7 * mm});
            skSolve(sketch);
        }
        {
            var Q0;
            Q0=qSketchRegion(id+"F4",true);
            extrude(context, id + "F5", {"entities" : qUnion([Q0]), "operationType" : NewBodyOperationType.ADD, "depth" : 1 * mm});
        }
        {
            var Q0;
            Q0=makeQuery(id+"F5.opExtrude","CAP_FACE",FACE,{"disambiguationData":[OSD([sQuery(id+"F4.wireOp",EDGE,"E43")])],"isStart":false});
            var sketch = newSketch(context, id + "F6", { "sketchPlane" : qUnion([Q0])});
            skCircle(sketch, "E44", {"center": v(0, 0) * mm, "radius": 2.6 * mm});
            skSolve(sketch);
        }
        {
            var Q0;
            Q0=qSketchRegion(id+"F6",true);
            extrude(context, id + "F7", {"entities" : qUnion([Q0]), "operationType" : NewBodyOperationType.REMOVE, "endBound" : BoundingType.THROUGH_ALL, "oppositeDirection" : true, "depth" : 25 * mm});
        }
        {
            var Q0;
            Q0=makeQuery(id+"F5.opExtrude","CAP_EDGE",EDGE,{"disambiguationData":[OSD([sQuery(id+"F4.wireOp",EDGE,"E43")])],"isStart":true});
            var Q1;
            Q1=makeQuery(id+"F3.opExtrude","CAP_EDGE",EDGE,{"disambiguationData":[OSD([sQuery(id+"F2.wireOp",EDGE,"E42")])],"isStart":true});
            chamfer(context, id + "F8", {"entities" : qUnion([Q0, Q1]), "width" : 1 * mm, "tangentPropagation" : true});
        }
    });
